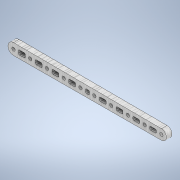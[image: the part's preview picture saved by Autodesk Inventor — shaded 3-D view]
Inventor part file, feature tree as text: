
AUTODESK INVENTOR PART (.ipt)
format: ipt  version: 2020.2 (Build 242310000, 310)  size: 263,680 bytes
history: native  units: mm
features: other x3, sketch x3, extrude x2, hole x1, fillet x1
ambient origin geometry x8: Origin, YZ Plane, XZ Plane, XY Plane, X Axis, Y Axis, Z Axis, Center Point
bodies: Body1 (feature_tree)
feature tree (10):
  other  "ソリッド1"
  sketch  "スケッチ1"
  extrude  "押し出し1"  Depth=132.465mm
  hole  "穴1"  [1 undecoded]
  sketch  "スケッチ2"
  extrude  "押し出し2"  Depth=9.0mm
  fillet  "フィレット1"  Radius=10.0mm
  sketch  "スケッチ3"
  other  "断面エッジを投影1"
  other  "断面エッジを投影2"
note: 1 required parameter value undecoded (feature->parameter linkage not recoverable at this tier; creation-order binding heuristic only, values carry confidence <= 0.55)
